# Revit family: FM-753EVOM20X263_120
name_source: partatom
category: Detail Items
revit_build: Autodesk Revit 2016 (Build: 20150220_1215(x64)
units: mm (PartAtom-declared; Revit-internal decimal feet)

## family parameters
OmniClass Number = 23.20.40.11.17.11
OmniClass Title = Expansion Anchors
Rotate with component = No
Shared = No

## types (2) — shared parameters
Density = 0.61 kg
Description = Metallic anchor
EPD = https://www.strongtie.eu
ETA / DoP = https://www.friulsider.com
Manufacturer = Friulsider
Model = FM-753 EVO M20X263/120
Model Disclaimer = Contact Simpson Strong-Tie Company  for more information
Model ID = 75340B20263
Name = FM-753 EVO M20X263/120
ObjectType = FM-753 EVO M20X263/120
Product Material = Galvanised
Product Type = Metallic anchor
Reference = 75340B20263
Technical datasheet = https://www.friulsider.com
URL = www.strongtie.eu
UniClass Number = Pr_20_29_03_97
UniClass Title = Wedge anchors

## per-type parameters (varying)
| type | _visiblefront | _visibletop |
| SST_FM-753 EVO M20X263/120_Front | Yes | No |
| SST_FM-753 EVO M20X263/120_Top | No | Yes |

## geometry (parser evidence)
native form markers: Blend x4, Sweep x1
no freeform markers — native parametric forms only
